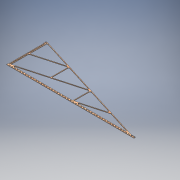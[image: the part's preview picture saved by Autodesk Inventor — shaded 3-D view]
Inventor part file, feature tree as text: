
AUTODESK INVENTOR PART (.ipt)
format: ipt  version: 2018.3 (Build 223284000, 284)  size: 503,808 bytes
history: native  units: mm
features: extrude x10, sketch x10, fillet x9, pattern_linear x1
ambient origin geometry x8: Origin, YZ Plane, XZ Plane, XY Plane, X Axis, Y Axis, Z Axis, Center Point
bodies: Solid1 (feature_tree)
feature tree (30):
  extrude  "Extrusion1"  Depth=250.0mm
  extrude  "Extrusion2"  TaperAngle=90.0deg  [1 undecoded]
  pattern_linear  "Rectangular Pattern1"  Count1=48 Spacing1=10.0mm
  extrude  "Extrusion3"  Depth=3.0mm
  extrude  "Extrusion4"  TaperAngle=90.0deg  [1 undecoded]
  fillet  "Fillet1"  [1 undecoded]
  extrude  "Extrusion5"  Depth=1.5875mm TaperAngle=0.0deg
  fillet  "Fillet2"  Radius=2.0mm
  extrude  "Extrusion6"  Depth=30.0mm
  fillet  "Fillet3"  Radius=1.5875mm
  extrude  "Extrusion7"  Depth=1.0mm
  extrude  "Extrusion8"  Depth=1.5875mm TaperAngle=0.0deg
  fillet  "Fillet4"  Radius=4.0mm
  fillet  "Fillet5"  Radius=1.5875mm
  extrude  "Extrusion9"  Depth=1.5875mm TaperAngle=0.0deg
  fillet  "Fillet6"  Radius=3.0mm
  fillet  "Fillet7"  Radius=2.0mm
  extrude  "Extrusion10"  Depth=1.5875mm TaperAngle=0.0deg
  fillet  "Fillet8"  Radius=4.0mm
  fillet  "Fillet9"  Radius=2.0mm
  sketch  "Sketch1"  dims[d2=2.0mm d4=250.0mm]
  sketch  "Sketch2"  dims[d5=2.0mm d7=90.0deg]
  sketch  "Sketch3"  dims[d8=1.5875mm d9=0.0mm]
  sketch  "Sketch4"  dims[d10=1.5875mm]
  sketch  "Sketch5"  dims[d11=6.0mm]
  sketch  "Sketch6"  dims[d12=3.0mm]
  sketch  "Sketch7"  dims[d13=1.5875mm d14=0.0mm]
  sketch  "Sketch8"  dims[d15=5.0mm d16=480.0mm d18=10.0mm]
  sketch  "Sketch9"  dims[d19=3.0mm d20=3.0mm]
  sketch  "Sketch10"  dims[d21=1.5875mm d22=0.0mm d24=90.0deg d25=90.0deg d26=1.5875mm d27=0.0mm d28=2.0mm d29=30.0mm d31=10.0mm d32=10.0mm d34=10.0mm d36=1.5875mm d37=0.0mm d38=1.0mm d41=1.5875mm d42=0.0mm d43=4.0mm d44=1.5875mm d45=0.0mm d48=1.5875mm d49=0.0mm d50=3.0mm d51=2.0mm d54=1.5875mm d55=0.0mm d56=4.0mm d57=2.0mm d60=1.5875mm d61=0.0mm d62=4.0mm d63=3.0mm]
note: 3 required parameter values undecoded (feature->parameter linkage not recoverable at this tier; creation-order binding heuristic only, values carry confidence <= 0.55)
